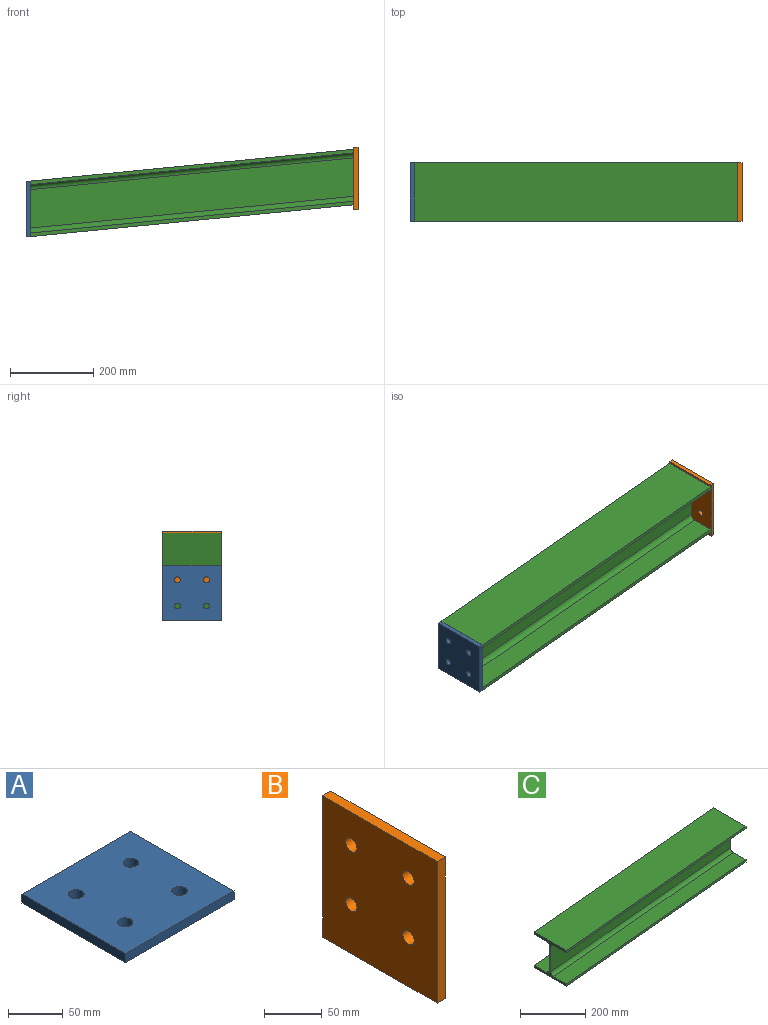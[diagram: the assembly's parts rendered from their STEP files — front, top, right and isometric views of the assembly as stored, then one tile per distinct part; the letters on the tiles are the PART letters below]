
ASSEMBLY  parts=3 mates=1
PART A: 10 faces, bbox 140x133x10 mm
  f0: cylinder r=7mm len=14mm, axis (0,0,-1), area 439.8mm2, adj f4,f5
  f1: cylinder r=7mm len=14mm, axis (0,0,-1), area 439.8mm2, adj f4,f5
  f2: cylinder r=7mm len=14mm, axis (0,0,-1), area 439.8mm2, adj f4,f5
  f3: cylinder r=7mm len=14mm, axis (0,0,-1), area 439.8mm2, adj f4,f5
  f4: plane 140x133mm, normal (0,0,1), area 18004.2mm2, adj f0,f1,f2,f3,f6,f7,f8,f9
  f5: plane 140x133mm, normal (0,0,-1), area 18004.2mm2, adj f0,f1,f2,f3,f6,f7,f8,f9
  f6: plane 133x10mm, normal (-1,0,0), area 1330mm2, adj f4,f5,f7,f9
  f7: plane 140x10mm, normal (0,-1,0), area 1400mm2, adj f4,f5,f6,f8
  f8: plane 133x10mm, normal (1,0,0), area 1330mm2, adj f4,f5,f7,f9
  f9: plane 140x10mm, normal (0,1,0), area 1400mm2, adj f4,f5,f6,f8
PART B: 10 faces, bbox 10x140x150 mm
  f0: plane 140x10mm, normal (0,0,1), area 1400mm2, adj f1,f7,f8,f9
  f1: plane 150x10mm, normal (0,-1,0), area 1500mm2, adj f0,f2,f8,f9
  f2: plane 140x10mm, normal (0,0,-1), area 1400mm2, adj f1,f7,f8,f9
  f3: cylinder r=7mm len=14mm, axis (1,0,0), area 439.8mm2, adj f8,f9
  f4: cylinder r=7mm len=14mm, axis (1,0,0), area 439.8mm2, adj f8,f9
  f5: cylinder r=7mm len=14mm, axis (1,0,0), area 439.8mm2, adj f8,f9
  f6: cylinder r=7mm len=14mm, axis (1,0,0), area 439.8mm2, adj f8,f9
  f7: plane 150x10mm, normal (0,1,0), area 1500mm2, adj f0,f2,f8,f9
  f8: plane 150x140mm, normal (-1,0,0), area 20384.2mm2, adj f0,f1,f2,f3,f4,f5,f6,f7
  f9: plane 150x140mm, normal (1,0,0), area 20384.2mm2, adj f0,f1,f2,f3,f4,f5,f6,f7
PART C: 18 faces, bbox 781.4x140x210.2 mm
  f0: plane 140x133.64mm, normal (-1,0,0), area 3156.7mm2, adj f1,f2,f3,f4,f5,f6,f7,f8
  f1: plane 779.05x85.09mm, normal (0,-1,0), area 6653.8mm2, adj f0,f2,f16,f17
  f2: plane 779.05x140mm, normal (-0.1,0,1), area 109592.3mm2, adj f0,f1,f3,f17
  f3: plane 779.05x85.09mm, normal (0,1,0), area 6653.8mm2, adj f0,f2,f4,f17
  f4: plane 779.05x76.55mm, normal (0.1,0,-1), area 43249.8mm2, adj f0,f3,f5,f17
  f5: cylinder r=12mm len=781.4mm, axis (1,0,0.1), area 14755.5mm2, adj f0,f4,f6,f17
  f6: plane 779.05x168.99mm, normal (0,1,0), area 72017.8mm2, adj f0,f5,f7,f17
  f7: cylinder r=12mm len=781.4mm, axis (1,0,0.1), area 14755.5mm2, adj f0,f6,f8,f17
  f8: plane 779.05x76.55mm, normal (-0.1,0,1), area 43249.8mm2, adj f0,f7,f9,f17
  f9: plane 779.05x85.09mm, normal (0,1,0), area 6653.8mm2, adj f0,f8,f10,f17
  f10: plane 779.05x140mm, normal (0.1,0,-1), area 109592.3mm2, adj f0,f9,f11,f17
  f11: plane 779.05x85.09mm, normal (0,-1,0), area 6653.8mm2, adj f0,f10,f12,f17
  f12: plane 779.05x76.55mm, normal (-0.1,0,1), area 43249.8mm2, adj f0,f11,f13,f17
  f13: cylinder r=12mm len=781.4mm, axis (1,0,0.1), area 14755.5mm2, adj f0,f12,f14,f17
  f14: plane 779.05x168.99mm, normal (0,-1,0), area 72017.8mm2, adj f0,f13,f15,f17
  f15: cylinder r=12mm len=781.4mm, axis (1,0,0.1), area 14755.5mm2, adj f0,f14,f16,f17
  f16: plane 779.05x76.55mm, normal (0.1,0,-1), area 43249.8mm2, adj f0,f1,f15,f17
  f17: plane 140x133.64mm, normal (1,0,0), area 3156.7mm2, adj f1,f2,f3,f4,f5,f6,f7,f8
PLACE A rot(axis=(0.58,0.58,0.58),120deg) t=(-802,-70,3871.67)mm fixed
PLACE B at identity
PLACE C t=(0,0,-0.01)mm
MATE fastened A.f4 <-> C.f0  axis (1,0,0) through (-792,0,3938.17)mm
